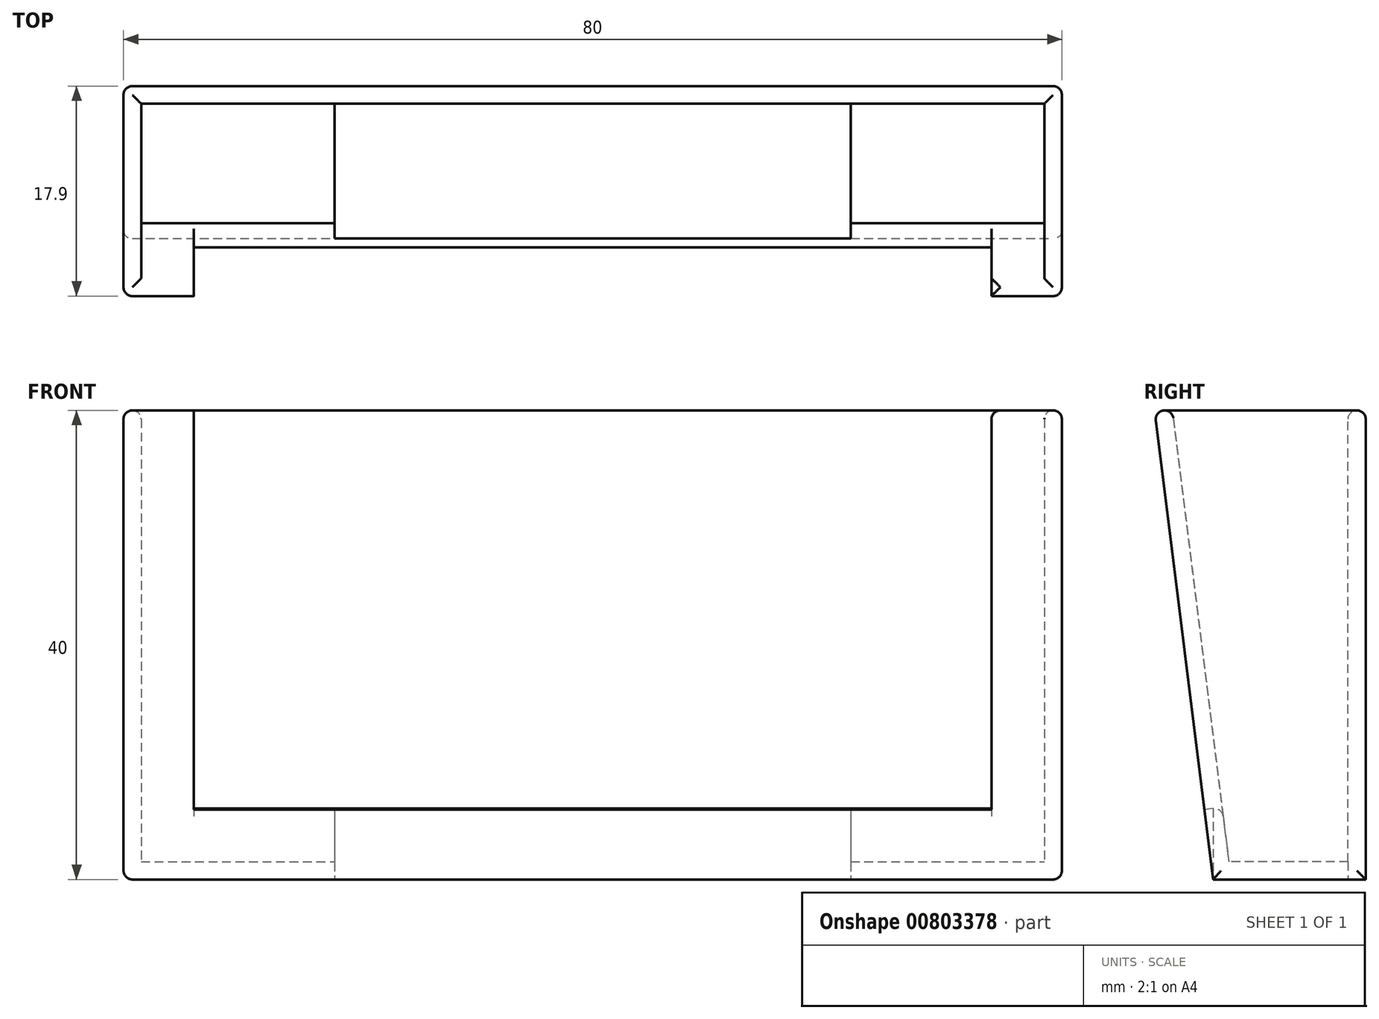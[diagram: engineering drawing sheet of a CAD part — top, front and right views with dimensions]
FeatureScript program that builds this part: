
annotation { "Feature Type Name" : "Feature", "Feature Type Description" : "" }
export const myFeature = defineFeature(function(context is Context, id is Id, definition is map)
    precondition{}
    {
        {
            var Q0;
            Q0=qCreatedBy(makeId("Top.planeOp"),FACE);
            var sketch = newSketch(context, id + "F0", { "sketchPlane" : qUnion([Q0])});
            skLineSegment(sketch, "E0.bottom", {"start": v(0, 0) * mm, "end": v(80, 0) * mm});
            skLineSegment(sketch, "E0.top", {"start": v(0, -13) * mm, "end": v(80, -13) * mm});
            skLineSegment(sketch, "E0.left", {"start": v(0, 0) * mm, "end": v(0, -13) * mm});
            skLineSegment(sketch, "E0.right", {"start": v(80, 0) * mm, "end": v(80, -13) * mm});
            skSolve(sketch);
        }
        {
            var Q0;
            Q0=qCreatedBy(makeId("Top.planeOp"),FACE);
            cPlane(context, id + "F1", {"entities" : qUnion([Q0]), "cplaneType" : CPlaneType.OFFSET, "offset" : 40 * mm, "width" : 150 * mm, "height" : 150 * mm});
        }
        {
            var Q0;
            Q0=qCreatedBy(id+"F1.planeOp",FACE);
            var sketch = newSketch(context, id + "F2", { "sketchPlane" : qUnion([Q0])});
            skLineSegment(sketch, "E1.bottom", {"start": v(0, 0) * mm, "end": v(80, 0) * mm});
            skLineSegment(sketch, "E1.top", {"start": v(0, -18) * mm, "end": v(80, -18) * mm});
            skLineSegment(sketch, "E1.left", {"start": v(0, 0) * mm, "end": v(0, -18) * mm});
            skLineSegment(sketch, "E1.right", {"start": v(80, 0) * mm, "end": v(80, -18) * mm});
            skSolve(sketch);
        }
        {
            var Q0;
            Q0=makeQuery(id+"F0.imprint","IMPRINT",FACE,{"disambiguationData":[TD([[makeQuery(id+"F0.imprint","IMPRINT",EDGE,{"derivedFrom":sQuery(id+"F0.wireOp",EDGE,"E0.bottom")}),-1.0]])]});
            var Q1;
            Q1=makeQuery(id+"F2.imprint","IMPRINT",FACE,{"disambiguationData":[TD([[makeQuery(id+"F2.imprint","IMPRINT",EDGE,{"derivedFrom":sQuery(id+"F2.wireOp",EDGE,"E1.bottom")}),-1.0]])]});
            loft(context, id + "F3", {"sheetProfilesArray" : [{ "sheetProfileEntities" : qUnion([Q0]) }, { "sheetProfileEntities" : qUnion([Q1]) }]});
        }
        {
            var Q0;
            Q0=makeQuery(id+"F3.opLoft","CAP_FACE",FACE,{"disambiguationData":[OSD([makeQuery(id+"F2.imprint","IMPRINT",FACE,{"disambiguationData":[TD([[makeQuery(id+"F2.imprint","IMPRINT",EDGE,{"derivedFrom":sQuery(id+"F2.wireOp",EDGE,"E1.bottom")}),-1.0]])]})])],"isStart":true});
            shell(context, id + "F4", {"entities" : qUnion([Q0]), "thickness" : 1.5 * mm});
        }
        {
            var Q0;
            Q0=makeQuery(id+"F3.opLoft","SWEPT_FACE",FACE,{"disambiguationData":[OSD([sQuery(id+"F0.wireOp",EDGE,"E0.top"),sQuery(id+"F0.wireOp",EDGE,"E0.left"),sQuery(id+"F0.wireOp",EDGE,"E0.right"),sQuery(id+"F2.wireOp",EDGE,"E1.top"),sQuery(id+"F2.wireOp",EDGE,"E1.left"),sQuery(id+"F2.wireOp",EDGE,"E1.right")])]});
            var sketch = newSketch(context, id + "F5", { "sketchPlane" : qUnion([Q0])});
            skLineSegment(sketch, "E2.bottom", {"start": v(6, 41.92) * mm, "end": v(74, 41.92) * mm});
            skLineSegment(sketch, "E2.top", {"start": v(6, 7.61) * mm, "end": v(74, 7.61) * mm});
            skLineSegment(sketch, "E2.left", {"start": v(6, 41.92) * mm, "end": v(6, 7.61) * mm});
            skLineSegment(sketch, "E2.right", {"start": v(74, 41.92) * mm, "end": v(74, 7.61) * mm});
            skSolve(sketch);
        }
        {
            var Q0;
            Q0 = qSketchRegion(id + "F5", true);
            extrude(context, id + "F6", {"entities" : qUnion([Q0]), "operationType" : NewBodyOperationType.REMOVE, "oppositeDirection" : true, "depth" : 2.7 * mm, "offsetDistance" : 25 * mm});
        }
        {
            var Q0;
            Q0=makeQuery(id+"F3.opLoft","CAP_FACE",FACE,{"disambiguationData":[OSD([makeQuery(id+"F0.imprint","IMPRINT",FACE,{"disambiguationData":[TD([[makeQuery(id+"F0.imprint","IMPRINT",EDGE,{"derivedFrom":sQuery(id+"F0.wireOp",EDGE,"E0.bottom")}),-1.0]])]})])],"isStart":true});
            var sketch = newSketch(context, id + "F7", { "sketchPlane" : qUnion([Q0])});
            skLineSegment(sketch, "E3.bottom", {"start": v(18, 13) * mm, "end": v(62, 13) * mm});
            skLineSegment(sketch, "E3.top", {"start": v(18, 1.5) * mm, "end": v(62, 1.5) * mm});
            skLineSegment(sketch, "E3.left", {"start": v(18, 13) * mm, "end": v(18, 1.5) * mm});
            skLineSegment(sketch, "E3.right", {"start": v(62, 13) * mm, "end": v(62, 1.5) * mm});
            skSolve(sketch);
        }
        {
            var Q0;
            Q0=makeQuery(id+"F7.imprint","IMPRINT",FACE,{"disambiguationData":[TD([[makeQuery(id+"F7.imprint","IMPRINT",EDGE,{"derivedFrom":sQuery(id+"F7.wireOp",EDGE,"E3.bottom")}),-1.0]])]});
            extrude(context, id + "F8", {"entities" : qUnion([Q0]), "operationType" : NewBodyOperationType.REMOVE, "oppositeDirection" : true, "depth" : 25 * mm, "offsetDistance" : 25 * mm});
        }
        {
            var Q0;
            Q0=makeQuery(id+"F3.opLoft","SWEPT_EDGE",EDGE,{"disambiguationData":[OSD([sQuery(id+"F0.wireOp",EDGE,"E0.top"),sQuery(id+"F0.wireOp",EDGE,"E0.right"),sQuery(id+"F2.wireOp",EDGE,"E1.top"),sQuery(id+"F2.wireOp",EDGE,"E1.right")])]});
            var Q1;
            Q1=makeQuery(id+"F3.opLoft","MID_CAP_EDGE",EDGE,{"disambiguationData":[OSD([sQuery(id+"F0.wireOp",EDGE,"E0.bottom"),sQuery(id+"F0.wireOp",EDGE,"E0.top"),sQuery(id+"F0.wireOp",EDGE,"E0.right")])],"capPos":0.0});
            var Q2;
            Q2=makeQuery(id+"F3.opLoft","SWEPT_EDGE",EDGE,{"disambiguationData":[OSD([sQuery(id+"F0.wireOp",EDGE,"E0.bottom"),sQuery(id+"F0.wireOp",EDGE,"E0.right"),sQuery(id+"F2.wireOp",EDGE,"E1.bottom"),sQuery(id+"F2.wireOp",EDGE,"E1.right")])]});
            var Q3;
            Q3=makeQuery(id+"F3.opLoft","SWEPT_EDGE",EDGE,{"disambiguationData":[OSD([sQuery(id+"F0.wireOp",EDGE,"E0.top"),sQuery(id+"F0.wireOp",EDGE,"E0.left"),sQuery(id+"F2.wireOp",EDGE,"E1.top"),sQuery(id+"F2.wireOp",EDGE,"E1.left")])]});
            var Q4;
            Q4=makeQuery(id+"F3.opLoft","SWEPT_EDGE",EDGE,{"disambiguationData":[OSD([sQuery(id+"F0.wireOp",EDGE,"E0.bottom"),sQuery(id+"F0.wireOp",EDGE,"E0.left"),sQuery(id+"F2.wireOp",EDGE,"E1.bottom"),sQuery(id+"F2.wireOp",EDGE,"E1.left")])]});
            var Q5;
            Q5=makeQuery(id+"F3.opLoft","MID_CAP_EDGE",EDGE,{"disambiguationData":[OSD([sQuery(id+"F0.wireOp",EDGE,"E0.bottom"),sQuery(id+"F0.wireOp",EDGE,"E0.top"),sQuery(id+"F0.wireOp",EDGE,"E0.left")])],"capPos":0.0});
            var Q6;
            Q6=makeQuery(id+"F6.boolean.opBoolean","COPY",EDGE,{"derivedFrom":makeQuery(id+"F6.opExtrude","CAP_EDGE",EDGE,{"disambiguationData":[OSD([sQuery(id+"F5.wireOp",EDGE,"E2.left")])],"isStart":true})});
            var Q7;
            Q7=makeQuery(id+"F6.boolean.opBoolean","COPY",EDGE,{"derivedFrom":makeQuery(id+"F6.opExtrude","CAP_EDGE",EDGE,{"disambiguationData":[OSD([sQuery(id+"F5.wireOp",EDGE,"E2.right")])],"isStart":true})});
            var Q8;
            {var subQ0=sQuery(id+"F2.wireOp",EDGE,"E1.right");var subQ1=sQuery(id+"F2.wireOp",EDGE,"E1.top");var subQ5=sQuery(id+"F2.wireOp",EDGE,"E1.left");Q8=makeQuery(id+"F6.boolean.opBoolean","SPLIT",EDGE,{"disambiguationData":[TD([makeQuery(id+"F6.opExtrude","SWEPT_FACE",FACE,{"disambiguationData":[OSD([sQuery(id+"F5.wireOp",EDGE,"E2.right")])]})])],"derivedFrom":makeQuery(id+"F3.opLoft","MID_CAP_EDGE",EDGE,{"disambiguationData":[OSD([subQ1,subQ5,subQ0])],"capPos":1.0})});}
            var Q9;
            Q9=makeQuery(id+"F3.opLoft","MID_CAP_EDGE",EDGE,{"disambiguationData":[OSD([sQuery(id+"F2.wireOp",EDGE,"E1.bottom"),sQuery(id+"F2.wireOp",EDGE,"E1.top"),sQuery(id+"F2.wireOp",EDGE,"E1.right")])],"capPos":1.0});
            var Q10;
            Q10=makeQuery(id+"F4.opShell","OFFSET_EDGE",EDGE,{"disambiguationData":[OSD([sQuery(id+"F2.wireOp",EDGE,"E1.bottom"),sQuery(id+"F2.wireOp",EDGE,"E1.top"),sQuery(id+"F2.wireOp",EDGE,"E1.right")])]});
            var Q11;
            {var subQ1=sQuery(id+"F2.wireOp",EDGE,"E1.top");var subQ2=sQuery(id+"F2.wireOp",EDGE,"E1.left");var subQ3=sQuery(id+"F2.wireOp",EDGE,"E1.right");Q11=makeQuery(id+"F6.boolean.opBoolean","SPLIT",EDGE,{"disambiguationData":[TD([makeQuery(id+"F6.opExtrude","SWEPT_FACE",FACE,{"disambiguationData":[OSD([sQuery(id+"F5.wireOp",EDGE,"E2.right")])]})])],"derivedFrom":makeQuery(id+"F4.opShell","OFFSET_EDGE",EDGE,{"disambiguationData":[OSD([subQ1,subQ2,subQ3])]})});}
            var Q12;
            Q12=makeQuery(id+"F6.boolean.opBoolean","INTERSECT",EDGE,{"derivedFrom":[makeQuery(id+"F3.opLoft","CAP_FACE",FACE,{"disambiguationData":[OSD([makeQuery(id+"F2.imprint","IMPRINT",FACE,{"disambiguationData":[TD([[makeQuery(id+"F2.imprint","IMPRINT",EDGE,{"derivedFrom":sQuery(id+"F2.wireOp",EDGE,"E1.bottom")}),-1.0]])]})])],"isStart":true}),makeQuery(id+"F6.opExtrude","SWEPT_FACE",FACE,{"disambiguationData":[OSD([sQuery(id+"F5.wireOp",EDGE,"E2.right")])]})]});
            var Q13;
            Q13=makeQuery(id+"F4.opShell","OFFSET_EDGE",EDGE,{"disambiguationData":[OSD([sQuery(id+"F2.wireOp",EDGE,"E1.bottom"),sQuery(id+"F2.wireOp",EDGE,"E1.left"),sQuery(id+"F2.wireOp",EDGE,"E1.right")])]});
            var Q14;
            Q14=makeQuery(id+"F4.opShell","OFFSET_EDGE",EDGE,{"disambiguationData":[OSD([sQuery(id+"F2.wireOp",EDGE,"E1.bottom"),sQuery(id+"F2.wireOp",EDGE,"E1.top"),sQuery(id+"F2.wireOp",EDGE,"E1.left")])]});
            var Q15;
            Q15=makeQuery(id+"F3.opLoft","MID_CAP_EDGE",EDGE,{"disambiguationData":[OSD([sQuery(id+"F2.wireOp",EDGE,"E1.bottom"),sQuery(id+"F2.wireOp",EDGE,"E1.top"),sQuery(id+"F2.wireOp",EDGE,"E1.left")])],"capPos":1.0});
            var Q16;
            {var subQ1=sQuery(id+"F2.wireOp",EDGE,"E1.top");var subQ2=sQuery(id+"F2.wireOp",EDGE,"E1.left");var subQ3=sQuery(id+"F2.wireOp",EDGE,"E1.right");Q16=makeQuery(id+"F6.boolean.opBoolean","SPLIT",EDGE,{"disambiguationData":[TD([makeQuery(id+"F6.opExtrude","SWEPT_FACE",FACE,{"disambiguationData":[OSD([sQuery(id+"F5.wireOp",EDGE,"E2.left")])]})])],"derivedFrom":makeQuery(id+"F4.opShell","OFFSET_EDGE",EDGE,{"disambiguationData":[OSD([subQ1,subQ2,subQ3])]})});}
            var Q17;
            {var subQ0=sQuery(id+"F2.wireOp",EDGE,"E1.left");var subQ1=sQuery(id+"F2.wireOp",EDGE,"E1.top");var subQ5=sQuery(id+"F2.wireOp",EDGE,"E1.right");Q17=makeQuery(id+"F6.boolean.opBoolean","SPLIT",EDGE,{"disambiguationData":[TD([makeQuery(id+"F6.opExtrude","SWEPT_FACE",FACE,{"disambiguationData":[OSD([sQuery(id+"F5.wireOp",EDGE,"E2.left")])]})])],"derivedFrom":makeQuery(id+"F3.opLoft","MID_CAP_EDGE",EDGE,{"disambiguationData":[OSD([subQ1,subQ0,subQ5])],"capPos":1.0})});}
            var Q18;
            Q18=makeQuery(id+"F3.opLoft","MID_CAP_EDGE",EDGE,{"disambiguationData":[OSD([sQuery(id+"F2.wireOp",EDGE,"E1.bottom"),sQuery(id+"F2.wireOp",EDGE,"E1.left"),sQuery(id+"F2.wireOp",EDGE,"E1.right")])],"capPos":1.0});
            var Q19;
            {var subQ0=makeQuery(id+"F4.opShell","OFFSET_FACE",FACE,{"disambiguationData":[OSD([sQuery(id+"F0.wireOp",EDGE,"E0.top"),sQuery(id+"F0.wireOp",EDGE,"E0.left"),sQuery(id+"F0.wireOp",EDGE,"E0.right"),sQuery(id+"F2.wireOp",EDGE,"E1.top"),sQuery(id+"F2.wireOp",EDGE,"E1.left"),sQuery(id+"F2.wireOp",EDGE,"E1.right")])]});var subQ1=makeQuery(id+"F6.opExtrude","SWEPT_FACE",FACE,{"disambiguationData":[OSD([sQuery(id+"F5.wireOp",EDGE,"E2.top")])]});Q19=makeQuery(id+"F8.boolean.opBoolean","SPLIT",EDGE,{"disambiguationData":[TD([makeQuery(id+"F6.boolean.opBoolean","COPY",FACE,{"derivedFrom":makeQuery(id+"F6.opExtrude","SWEPT_FACE",FACE,{"disambiguationData":[OSD([sQuery(id+"F5.wireOp",EDGE,"E2.left")])]})})])],"derivedFrom":makeQuery(id+"F6.boolean.opBoolean","INTERSECT",EDGE,{"derivedFrom":[subQ0,subQ1]})});}
            var Q20;
            {var subQ0=makeQuery(id+"F4.opShell","OFFSET_FACE",FACE,{"disambiguationData":[OSD([sQuery(id+"F0.wireOp",EDGE,"E0.top"),sQuery(id+"F0.wireOp",EDGE,"E0.left"),sQuery(id+"F0.wireOp",EDGE,"E0.right"),sQuery(id+"F2.wireOp",EDGE,"E1.top"),sQuery(id+"F2.wireOp",EDGE,"E1.left"),sQuery(id+"F2.wireOp",EDGE,"E1.right")])]});var subQ1=makeQuery(id+"F6.opExtrude","SWEPT_FACE",FACE,{"disambiguationData":[OSD([sQuery(id+"F5.wireOp",EDGE,"E2.top")])]});Q20=makeQuery(id+"F8.boolean.opBoolean","SPLIT",EDGE,{"disambiguationData":[TD([makeQuery(id+"F6.boolean.opBoolean","COPY",FACE,{"derivedFrom":makeQuery(id+"F6.opExtrude","SWEPT_FACE",FACE,{"disambiguationData":[OSD([sQuery(id+"F5.wireOp",EDGE,"E2.right")])]})})])],"derivedFrom":makeQuery(id+"F6.boolean.opBoolean","INTERSECT",EDGE,{"derivedFrom":[subQ0,subQ1]})});}
            fillet(context, id + "F9", {"entities" : qUnion([Q0, Q1, Q2, Q3, Q4, Q5, Q6, Q7, Q8, Q9, Q10, Q11, Q12, Q13, Q14, Q15, Q16, Q17, Q18, Q19, Q20]), "radius" : 0.75 * mm, "tangentPropagation" : true, "allowEdgeOverflow" : false});
        }
    });
